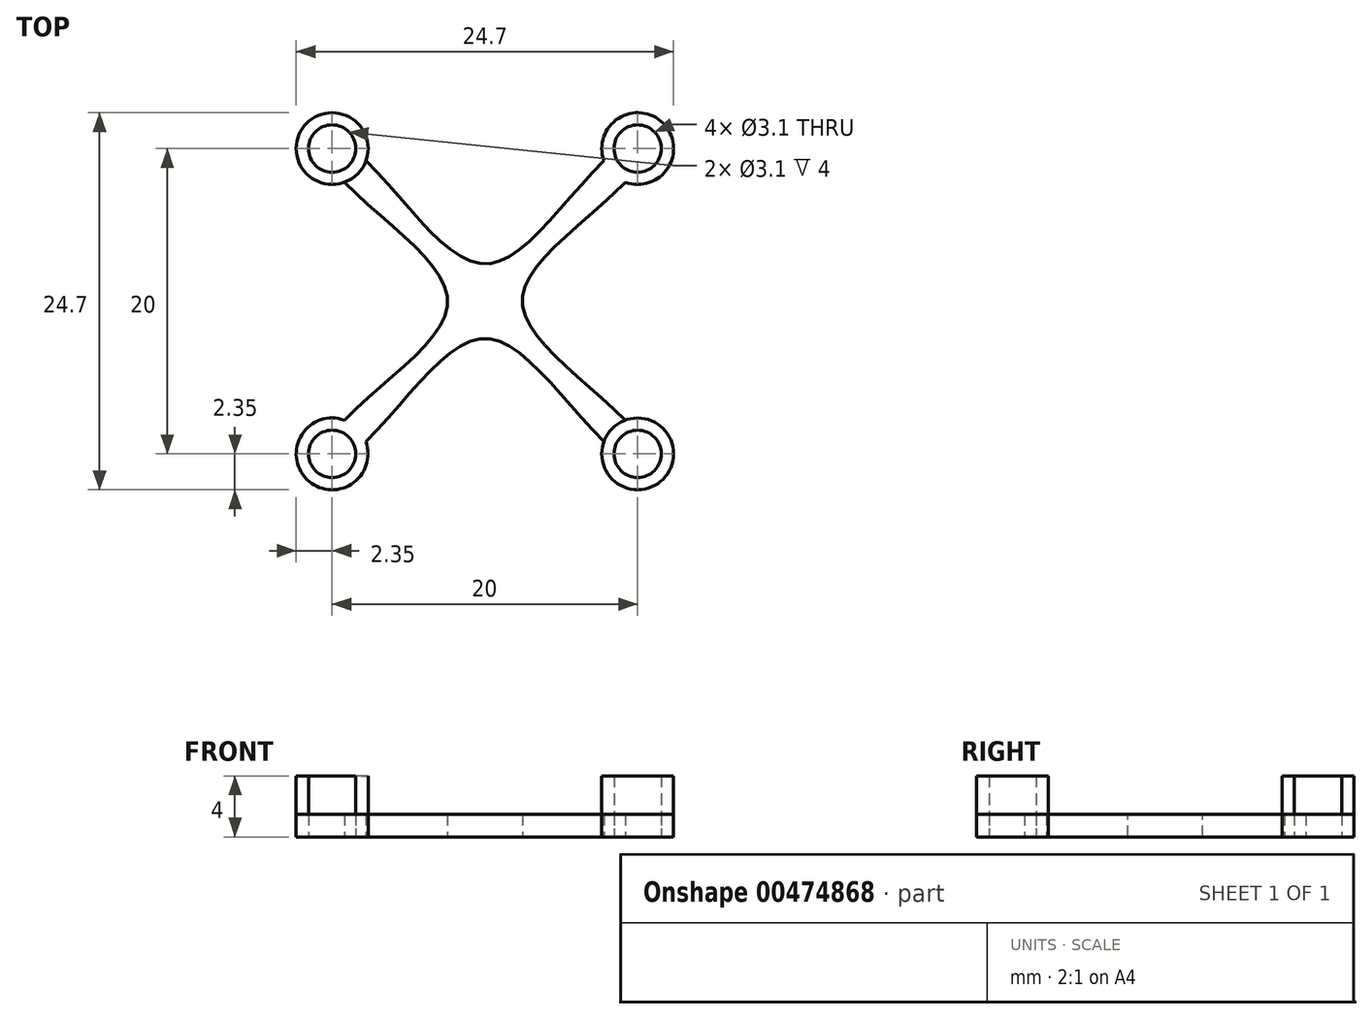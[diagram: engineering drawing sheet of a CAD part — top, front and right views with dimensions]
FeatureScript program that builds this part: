
annotation { "Feature Type Name" : "Feature", "Feature Type Description" : "" }
export const myFeature = defineFeature(function(context is Context, id is Id, definition is map)
    precondition{}
    {
        {
            var Q0;
            Q0=qCreatedBy(makeId("Top.planeOp"),FACE);
            var sketch = newSketch(context, id + "F0", { "sketchPlane" : qUnion([Q0])});
            skLineSegment(sketch, "E0.bottom", {"start": v(10, -10) * mm, "end": v(-10, -10) * mm, "construction": true});
            skLineSegment(sketch, "E0.top", {"start": v(10, 10) * mm, "end": v(-10, 10) * mm, "construction": true});
            skLineSegment(sketch, "E0.left", {"start": v(10, -10) * mm, "end": v(10, 10) * mm, "construction": true});
            skLineSegment(sketch, "E0.right", {"start": v(-10, -10) * mm, "end": v(-10, 10) * mm, "construction": true});
            skPoint(sketch, "E0.middle", {"position": v(0, 0) * mm});
            skCircle(sketch, "E1", {"center": v(-10, 10) * mm, "radius": 1.55 * mm});
            skCircle(sketch, "E2.0", {"center": v(-10, 10) * mm, "radius": 2.35 * mm});
            skCircle(sketch, "E3.MirrorC", {"center": v(10, 10) * mm, "radius": 2.35 * mm});
            skCircle(sketch, "E4.MirrorC", {"center": v(10, 10) * mm, "radius": 1.55 * mm});
            skCircle(sketch, "E5.MirrorC", {"center": v(-10, -10) * mm, "radius": 2.35 * mm});
            skCircle(sketch, "E6.MirrorC", {"center": v(-10, -10) * mm, "radius": 1.55 * mm});
            skCircle(sketch, "E7.MirrorC", {"center": v(10, -10) * mm, "radius": 2.35 * mm});
            skCircle(sketch, "E8.MirrorC", {"center": v(10, -10) * mm, "radius": 1.55 * mm});
            skLineSegment(sketch, "E9", {"start": v(-10, 10) * mm, "end": v(10, -10) * mm, "construction": true});
            skLineSegment(sketch, "E10", {"start": v(-10, -10) * mm, "end": v(10, 10) * mm, "construction": true});
            skLineSegment(sketch, "E11", {"start": v(0, 10) * mm, "end": v(0, -10) * mm, "construction": true});
            skLineSegment(sketch, "E12", {"start": v(-10, 0) * mm, "end": v(10, 0) * mm, "construction": true});
            skLineSegment(sketch, "E13.0", {"start": v(-10.7, 9.3) * mm, "end": v(9.3, -10.7) * mm, "construction": true});
            skLineSegment(sketch, "E14.0", {"start": v(-9.3, 10.7) * mm, "end": v(10.7, -9.3) * mm, "construction": true});
            skLineSegment(sketch, "E15.0", {"start": v(-9.3, -10.7) * mm, "end": v(10.7, 9.3) * mm, "construction": true});
            skLineSegment(sketch, "E16.0", {"start": v(-10.7, -9.3) * mm, "end": v(9.3, 10.7) * mm, "construction": true});
            skFitSpline(sketch, "E17", {"points": [v(-7.79, 9.2) * mm, v(0, 2.45) * mm, v(7.79, 9.2) * mm], "startDerivative": vector(17.05, -17.05) * mm, "endDerivative": vector(17.34, 17.34) * mm});
            skFitSpline(sketch, "E18.MirrorCS", {"points": [v(-9.2, 7.79) * mm, v(-2.45, 0) * mm, v(-9.2, -7.79) * mm], "startDerivative": vector(17.05, -17.05) * mm, "endDerivative": vector(-17.34, -17.34) * mm});
            skFitSpline(sketch, "E19.MirrorCS", {"points": [v(7.79, -9.2) * mm, v(0, -2.45) * mm, v(-7.79, -9.2) * mm], "startDerivative": vector(-17.05, 17.05) * mm, "endDerivative": vector(-17.34, -17.34) * mm});
            skFitSpline(sketch, "E20.MirrorCS", {"points": [v(9.2, -7.79) * mm, v(2.45, 0) * mm, v(9.2, 7.79) * mm], "startDerivative": vector(-17.05, 17.05) * mm, "endDerivative": vector(17.34, 17.34) * mm});
            skSolve(sketch);
        }
        {
            var Q0;
            Q0=makeQuery(id+"F0.imprint","IMPRINT",FACE,{"disambiguationData":[TD([[makeQuery(id+"F0.imprint","IMPRINT",EDGE,{"derivedFrom":sQuery(id+"F0.wireOp",EDGE,"E4.MirrorC")}),1.0]])]});
            var Q1;
            Q1=makeQuery(id+"F0.imprint","IMPRINT",FACE,{"disambiguationData":[TD([[makeQuery(id+"F0.imprint","IMPRINT",EDGE,{"derivedFrom":sQuery(id+"F0.wireOp",EDGE,"E6.MirrorC")}),1.0]])]});
            var Q2;
            Q2=makeQuery(id+"F0.imprint","IMPRINT",FACE,{"disambiguationData":[TD([[makeQuery(id+"F0.imprint","IMPRINT",EDGE,{"derivedFrom":sQuery(id+"F0.wireOp",EDGE,"E8.MirrorC")}),-1.0]])]});
            var Q3;
            Q3=makeQuery(id+"F0.imprint","IMPRINT",FACE,{"disambiguationData":[TD([[makeQuery(id+"F0.imprint","IMPRINT",EDGE,{"derivedFrom":sQuery(id+"F0.wireOp",EDGE,"E1")}),-1.0]])]});
            extrude(context, id + "F1", {"entities" : qUnion([Q0, Q1, Q2, Q3]), "depth" : 4 * mm});
        }
        {
            var Q0;
            Q0 = qSketchRegion(id + "F0", true);
            extrude(context, id + "F2", {"entities" : qUnion([Q0]), "depth" : 1.5 * mm});
        }
    });
